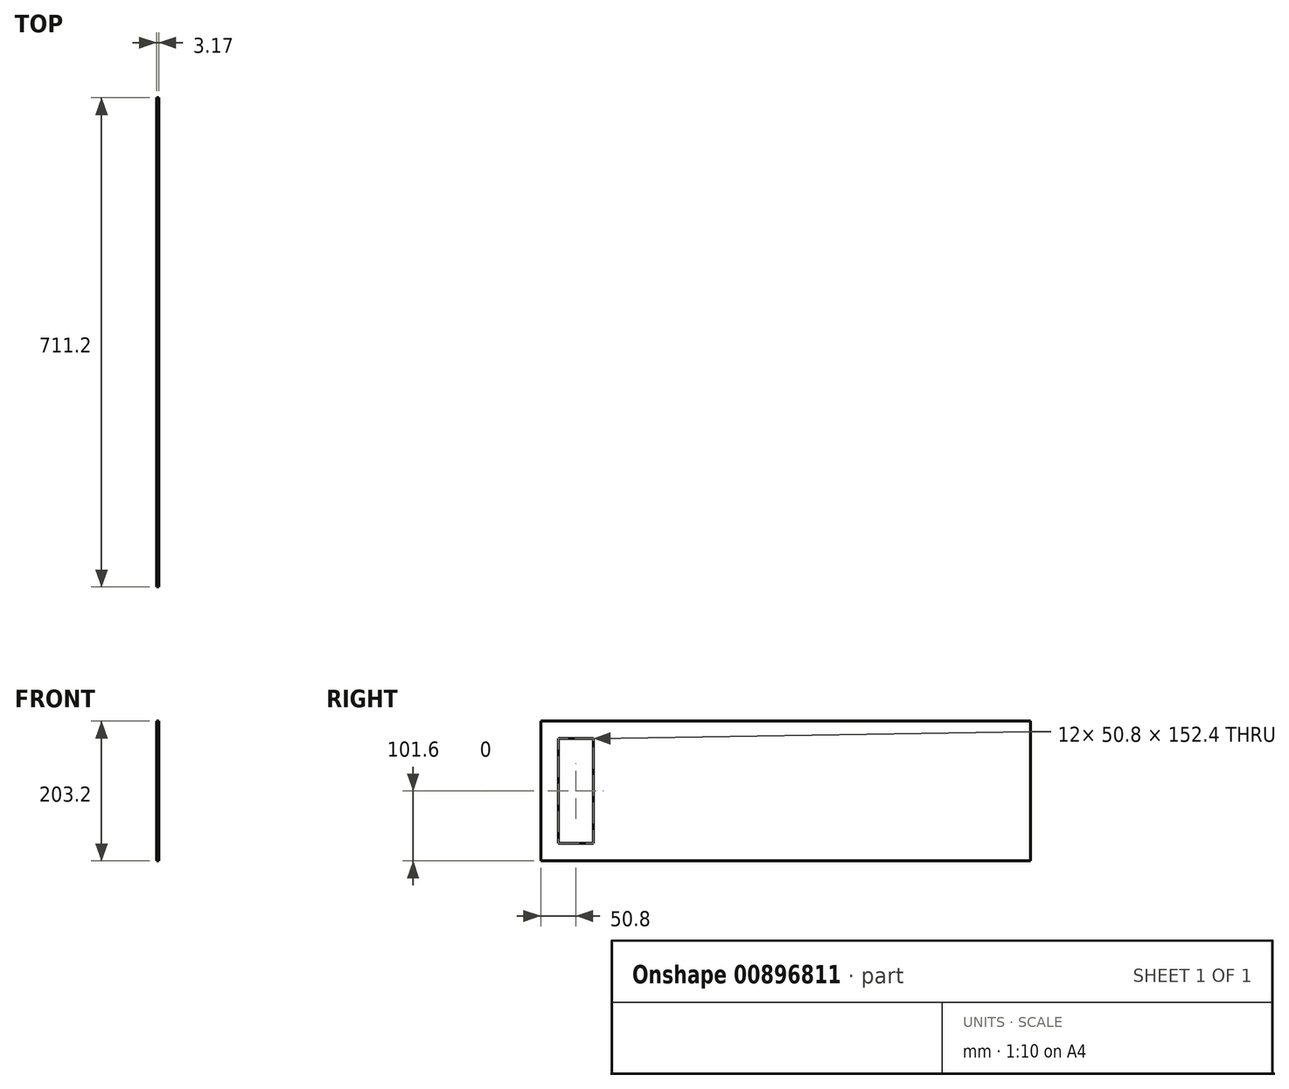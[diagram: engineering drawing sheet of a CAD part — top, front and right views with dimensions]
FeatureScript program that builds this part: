
annotation { "Feature Type Name" : "Feature", "Feature Type Description" : "" }
export const myFeature = defineFeature(function(context is Context, id is Id, definition is map)
    precondition{}
    {
        {
            var Q0;
            Q0=qCreatedBy(makeId("Right.planeOp"),FACE);
            var sketch = newSketch(context, id + "F0", { "sketchPlane" : qUnion([Q0])});
            skLineSegment(sketch, "E0.bottom", {"start": v(355.6, -101.6) * mm, "end": v(-355.6, -101.6) * mm});
            skLineSegment(sketch, "E0.top", {"start": v(355.6, 101.6) * mm, "end": v(-355.6, 101.6) * mm});
            skLineSegment(sketch, "E0.left", {"start": v(355.6, -101.6) * mm, "end": v(355.6, 101.6) * mm});
            skLineSegment(sketch, "E0.right", {"start": v(-355.6, -101.6) * mm, "end": v(-355.6, 101.6) * mm});
            skPoint(sketch, "E0.middle", {"position": v(0, 0) * mm});
            skLineSegment(sketch, "E1.bottom", {"start": v(-330.2, 76.2) * mm, "end": v(-279.4, 76.2) * mm});
            skLineSegment(sketch, "E1.top", {"start": v(-330.2, -76.2) * mm, "end": v(-279.4, -76.2) * mm});
            skLineSegment(sketch, "E1.left", {"start": v(-330.2, 76.2) * mm, "end": v(-330.2, -76.2) * mm});
            skLineSegment(sketch, "E1.right", {"start": v(-279.4, 76.2) * mm, "end": v(-279.4, -76.2) * mm});
            skSolve(sketch);
        }
        {
            var Q0;
            Q0 = qSketchRegion(id + "F0", true);
            extrude(context, id + "F1", {"entities" : qUnion([Q0]), "depth" : 3.17 * mm, "offsetDistance" : 25.4 * mm});
        }
    });
